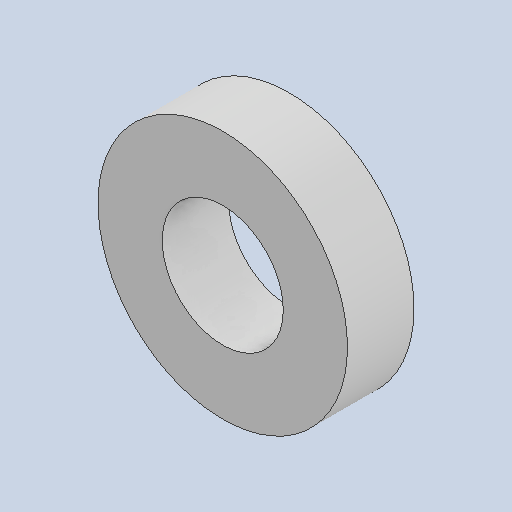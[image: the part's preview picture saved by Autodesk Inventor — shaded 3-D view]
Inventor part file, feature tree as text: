
AUTODESK INVENTOR PART (.ipt)
format: ipt  version: 2023 (Build 270158000, 158)  size: 139,776 bytes
history: native  units: in
note: dims shown in document units (in); Inventor stores cm internally (conversion verified against a paired STEP export)
features: extrude x1, sketch x1
ambient origin geometry x8: Origin, YZ Plane, XZ Plane, XY Plane, X Axis, Y Axis, Z Axis, Center Point
bodies: Solid1 (feature_tree)
feature tree (2):
  extrude  "Extrusion1"  Depth=0.1in
  sketch  "Sketch1"  dims[d0=0.126in d1=0.126in d2=0.182in d3=0.375in d4=0.1in d5=0.0in]
